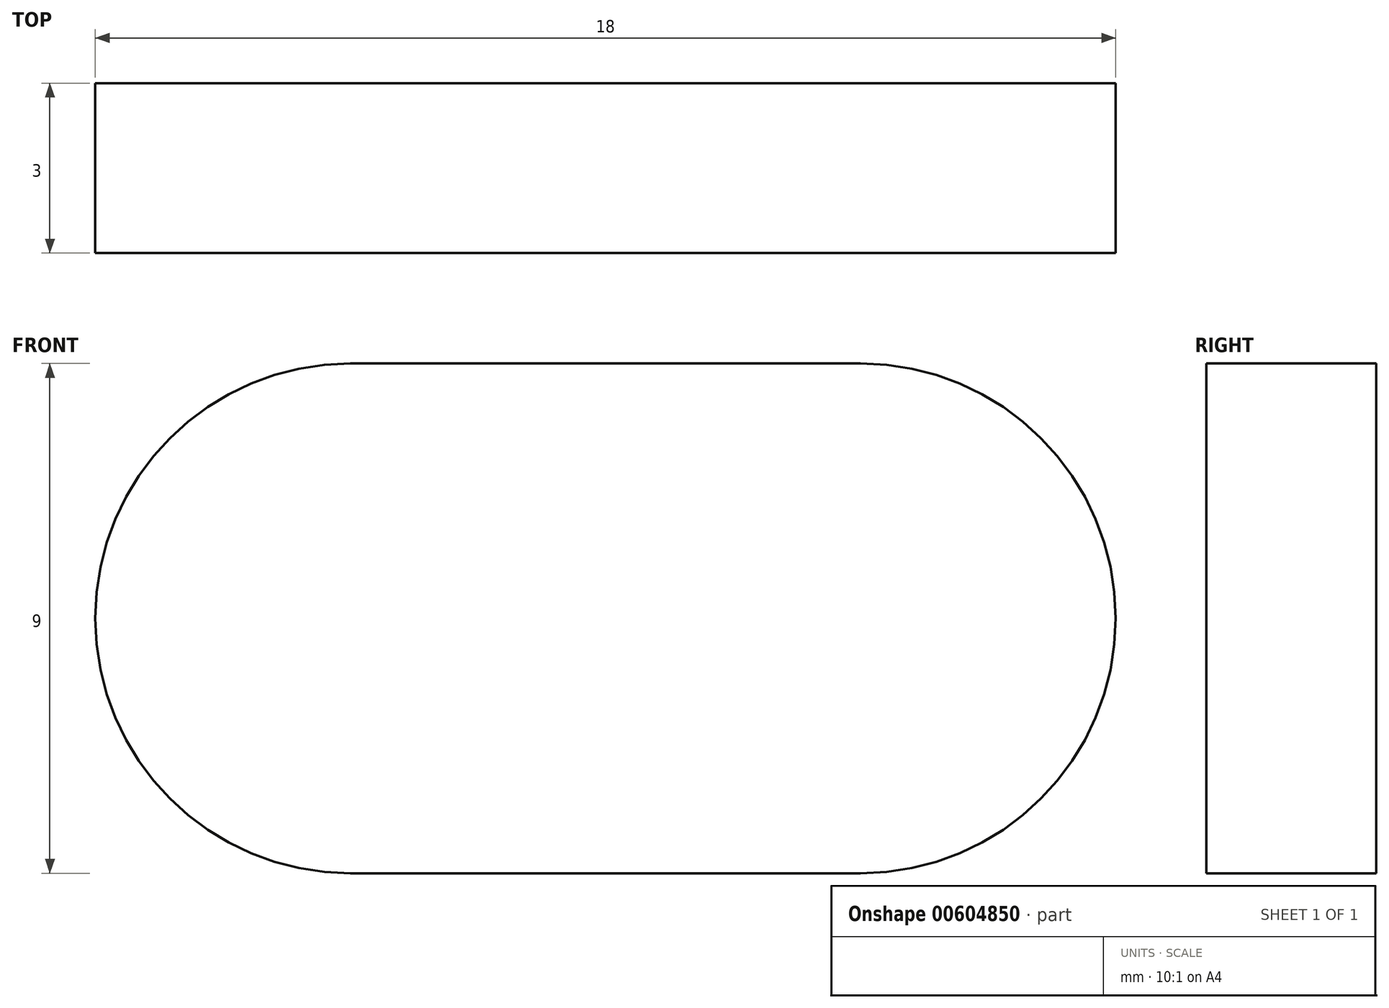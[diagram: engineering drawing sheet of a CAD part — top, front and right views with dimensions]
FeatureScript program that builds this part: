
annotation { "Feature Type Name" : "Feature", "Feature Type Description" : "" }
export const myFeature = defineFeature(function(context is Context, id is Id, definition is map)
    precondition{}
    {
        {
            var Q0;
            Q0=qCreatedBy(makeId("Front.planeOp"),FACE);
            var sketch = newSketch(context, id + "F0", { "sketchPlane" : qUnion([Q0])});
            skLineSegment(sketch, "E0.bottom", {"start": v(47, 24) * mm, "end": v(-47, 24) * mm});
            skLineSegment(sketch, "E0.top", {"start": v(47, -24) * mm, "end": v(-47, -24) * mm});
            skLineSegment(sketch, "E0.left", {"start": v(50, 21) * mm, "end": v(50, -21) * mm});
            skLineSegment(sketch, "E0.right", {"start": v(-50, 21) * mm, "end": v(-50, -21) * mm});
            skPoint(sketch, "E0.middle", {"position": v(0, 0) * mm});
            skPoint(sketch, "E1.visualSharp", {"position": v(-50, 24) * mm});
            skArc(sketch, "E1.filletArc", {"start": v(-47, 24) * mm, "mid": v(-49.12, 23.12) * mm, "end": v(-50, 21) * mm});
            skPoint(sketch, "E2.visualSharp", {"position": v(50, 24) * mm});
            skArc(sketch, "E2.filletArc", {"start": v(50, 21) * mm, "mid": v(49.12, 23.12) * mm, "end": v(47, 24) * mm});
            skPoint(sketch, "E3.visualSharp", {"position": v(50, -24) * mm});
            skArc(sketch, "E3.filletArc", {"start": v(47, -24) * mm, "mid": v(49.12, -23.12) * mm, "end": v(50, -21) * mm});
            skPoint(sketch, "E4.visualSharp", {"position": v(-50, -24) * mm});
            skArc(sketch, "E4.filletArc", {"start": v(-50, -21) * mm, "mid": v(-49.12, -23.12) * mm, "end": v(-47, -24) * mm});
            skSolve(sketch);
        }
        {
            var Q0;
            Q0 = qSketchRegion(id + "F0", true);
            extrude(context, id + "F1", {"entities" : qUnion([Q0]), "depth" : 3 * mm, "offsetDistance" : 25 * mm});
        }
        {
            var Q0;
            Q0=makeQuery(id+"F1.opExtrude","CAP_FACE",FACE,{"disambiguationData":[OSD([sQuery(id+"F0.wireOp",EDGE,"E0.bottom"),sQuery(id+"F0.wireOp",EDGE,"E0.top"),sQuery(id+"F0.wireOp",EDGE,"E0.left"),sQuery(id+"F0.wireOp",EDGE,"E0.right"),sQuery(id+"F0.wireOp",EDGE,"E1.filletArc"),sQuery(id+"F0.wireOp",EDGE,"E2.filletArc"),sQuery(id+"F0.wireOp",EDGE,"E3.filletArc"),sQuery(id+"F0.wireOp",EDGE,"E4.filletArc")])],"isStart":false});
            var sketch = newSketch(context, id + "F2", { "sketchPlane" : qUnion([Q0])});
            skLineSegment(sketch, "E5.bottom", {"start": v(39.5, -4.5) * mm, "end": v(30.5, -4.5) * mm});
            skLineSegment(sketch, "E5.top", {"start": v(39.5, 4.5) * mm, "end": v(30.5, 4.5) * mm});
            skPoint(sketch, "E5.middle", {"position": v(35, 0) * mm});
            skArc(sketch, "E6", {"start": v(39.5, -4.5) * mm, "mid": v(44, 0) * mm, "end": v(39.5, 4.5) * mm});
            skArc(sketch, "E7", {"start": v(30.5, 4.5) * mm, "mid": v(26, 0) * mm, "end": v(30.5, -4.5) * mm});
            skLineSegment(sketch, "E8", {"start": v(30.5, 4.5) * mm, "end": v(30.5, 0) * mm, "construction": true});
            skLineSegment(sketch, "E9", {"start": v(39.5, 4.5) * mm, "end": v(39.5, 0) * mm, "construction": true});
            skLineSegment(sketch, "E10.MirrorCS", {"start": v(-30.5, 4.5) * mm, "end": v(-30.5, 0) * mm, "construction": true});
            skLineSegment(sketch, "E11.MirrorCS", {"start": v(-39.5, 4.5) * mm, "end": v(-39.5, 0) * mm, "construction": true});
            skArc(sketch, "E12.MirrorCS", {"start": v(-30.5, 4.5) * mm, "mid": v(-26, 0) * mm, "end": v(-30.5, -4.5) * mm});
            skArc(sketch, "E13.MirrorCS", {"start": v(-39.5, -4.5) * mm, "mid": v(-44, 0) * mm, "end": v(-39.5, 4.5) * mm});
            skLineSegment(sketch, "E14.MirrorCS", {"start": v(-39.5, 4.5) * mm, "end": v(-30.5, 4.5) * mm});
            skLineSegment(sketch, "E15.MirrorCS", {"start": v(-39.5, -4.5) * mm, "end": v(-30.5, -4.5) * mm});
            skPoint(sketch, "E16.MirrorP", {"position": v(-35, 0) * mm});
            skSolve(sketch);
        }
        {
            var Q0;
            Q0=makeQuery(id+"F2.imprint","IMPRINT",FACE,{"disambiguationData":[TD([[makeQuery(id+"F2.imprint","IMPRINT",EDGE,{"derivedFrom":sQuery(id+"F2.wireOp",EDGE,"E5.bottom")}),-1.0]])]});
            var Q1;
            Q1=makeQuery(id+"F2.imprint","IMPRINT",FACE,{"disambiguationData":[TD([[makeQuery(id+"F2.imprint","IMPRINT",EDGE,{"derivedFrom":sQuery(id+"F2.wireOp",EDGE,"E12.MirrorCS")}),-1.0]])]});
            extrude(context, id + "F3", {"entities" : qUnion([Q0, Q1]), "operationType" : NewBodyOperationType.REMOVE, "oppositeDirection" : true, "depth" : 25 * mm, "offsetDistance" : 25 * mm});
        }
    });
